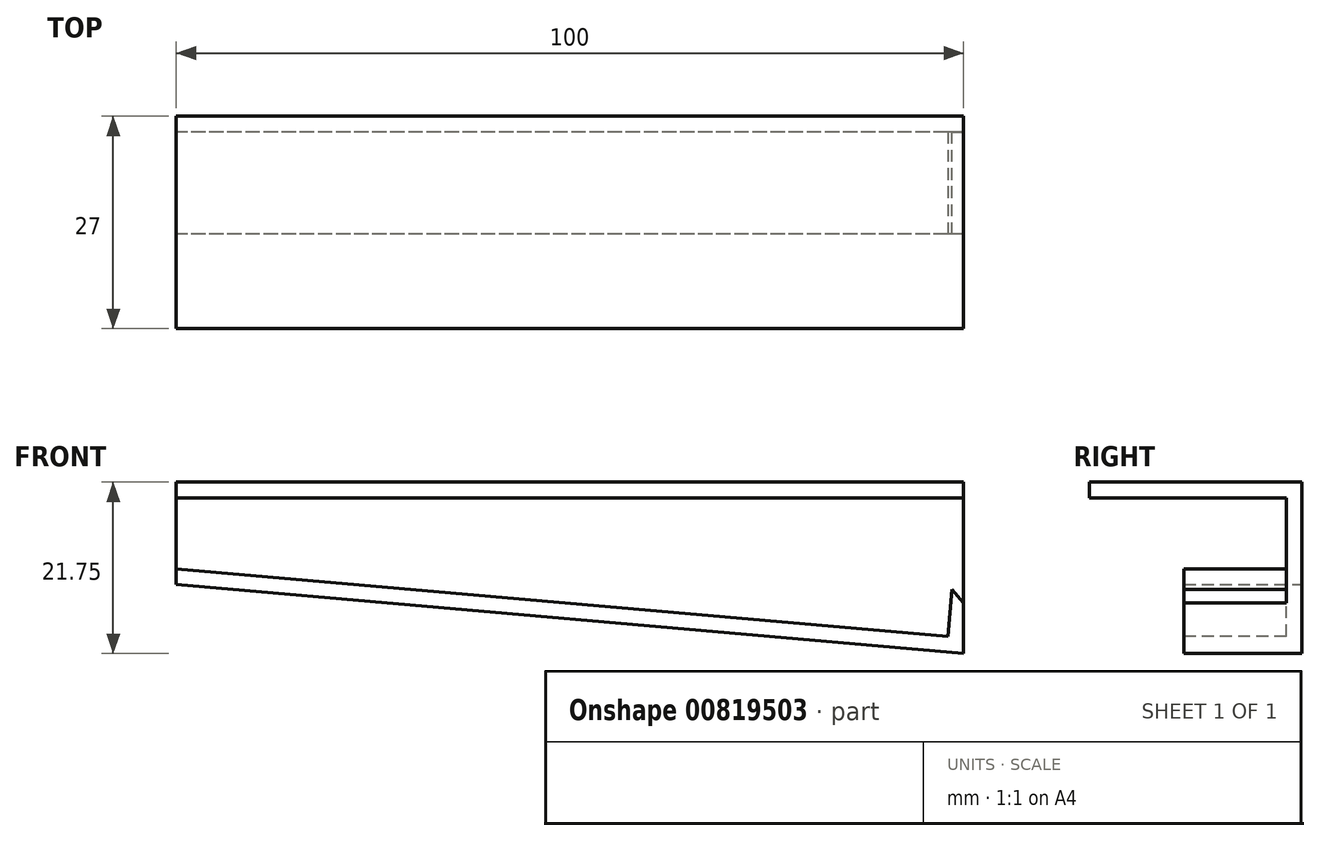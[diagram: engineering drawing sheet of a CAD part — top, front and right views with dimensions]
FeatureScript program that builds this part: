
annotation { "Feature Type Name" : "Feature", "Feature Type Description" : "" }
export const myFeature = defineFeature(function(context is Context, id is Id, definition is map)
    precondition{}
    {
        {
            var Q0;
            Q0=qCreatedBy(makeId("Front.planeOp"),FACE);
            var sketch = newSketch(context, id + "F0", { "sketchPlane" : qUnion([Q0])});
            skLineSegment(sketch, "E0", {"start": v(-26.66, 0) * mm, "end": v(-26.66, 13) * mm});
            skLineSegment(sketch, "E1", {"start": v(-26.66, 13) * mm, "end": v(73.34, 13) * mm});
            skLineSegment(sketch, "E2", {"start": v(73.34, 13) * mm, "end": v(73.34, -8.75) * mm});
            skLineSegment(sketch, "E3", {"start": v(73.34, -8.75) * mm, "end": v(-26.66, 0) * mm});
            skLineSegment(sketch, "E4", {"start": v(-26.66, 0) * mm, "end": v(38.37, 0) * mm, "construction": true});
            skSolve(sketch);
        }
        {
            var Q0;
            Q0=makeQuery(id+"F0.imprint","IMPRINT",FACE,{"disambiguationData":[TD([[makeQuery(id+"F0.imprint","IMPRINT",EDGE,{"derivedFrom":sQuery(id+"F0.wireOp",EDGE,"E0")}),-1.0]])]});
            extrude(context, id + "F1", {"entities" : qUnion([Q0]), "depth" : 2 * mm, "offsetDistance" : 25 * mm});
        }
        {
            var Q0;
            Q0=makeQuery(id+"F1.opExtrude","CAP_FACE",FACE,{"disambiguationData":[OSD([sQuery(id+"F0.wireOp",EDGE,"E0"),sQuery(id+"F0.wireOp",EDGE,"E1"),sQuery(id+"F0.wireOp",EDGE,"E2"),sQuery(id+"F0.wireOp",EDGE,"E3")])],"isStart":false});
            var sketch = newSketch(context, id + "F2", { "sketchPlane" : qUnion([Q0])});
            skLineSegment(sketch, "E5", {"start": v(-26.66, 13) * mm, "end": v(73.34, 13) * mm});
            skLineSegment(sketch, "E6", {"start": v(73.34, 13) * mm, "end": v(73.34, 11) * mm});
            skLineSegment(sketch, "E7", {"start": v(73.34, 11) * mm, "end": v(-26.66, 11) * mm});
            skLineSegment(sketch, "E8", {"start": v(-26.66, 11) * mm, "end": v(-26.66, 13) * mm});
            skLineSegment(sketch, "E9.0", {"start": v(73.34, -6.74) * mm, "end": v(-26.66, 2) * mm});
            skLineSegment(sketch, "E10", {"start": v(73.34, -6.74) * mm, "end": v(73.34, -8.75) * mm});
            skLineSegment(sketch, "E11", {"start": v(73.34, -8.75) * mm, "end": v(-26.66, 0) * mm});
            skLineSegment(sketch, "E12", {"start": v(-26.66, 0) * mm, "end": v(-26.66, 2) * mm});
            skSolve(sketch);
        }
        {
            var Q0;
            Q0=makeQuery(id+"F2.imprint","IMPRINT",FACE,{"disambiguationData":[TD([[makeQuery(id+"F2.imprint","IMPRINT",EDGE,{"derivedFrom":sQuery(id+"F2.wireOp",EDGE,"E9.0")}),1.0]])]});
            extrude(context, id + "F3", {"entities" : qUnion([Q0]), "operationType" : NewBodyOperationType.ADD, "depth" : 13 * mm, "offsetDistance" : 25 * mm});
        }
        {
            var Q0;
            Q0=makeQuery(id+"F2.imprint","IMPRINT",FACE,{"disambiguationData":[TD([[makeQuery(id+"F2.imprint","IMPRINT",EDGE,{"derivedFrom":sQuery(id+"F2.wireOp",EDGE,"E5")}),-1.0]])]});
            extrude(context, id + "F4", {"entities" : qUnion([Q0]), "operationType" : NewBodyOperationType.ADD, "depth" : 25 * mm, "offsetDistance" : 25 * mm});
        }
        {
            var Q0;
            Q0=makeQuery(id+"F3.opExtrude","SWEPT_FACE",FACE,{"disambiguationData":[OSD([sQuery(id+"F2.wireOp",EDGE,"E9.0")])]});
            var sketch = newSketch(context, id + "F5", { "sketchPlane" : qUnion([Q0])});
            skLineSegment(sketch, "E13.bottom", {"start": v(73.64, -2) * mm, "end": v(71.66, -2) * mm});
            skLineSegment(sketch, "E13.top", {"start": v(73.64, -15) * mm, "end": v(71.66, -15) * mm});
            skLineSegment(sketch, "E13.left", {"start": v(73.64, -2) * mm, "end": v(73.64, -15) * mm});
            skLineSegment(sketch, "E13.right", {"start": v(71.66, -2) * mm, "end": v(71.66, -15) * mm});
            skSolve(sketch);
        }
        {
            var Q0;
            Q0=makeQuery(id+"F5.imprint","IMPRINT",FACE,{"disambiguationData":[TD([[makeQuery(id+"F5.imprint","IMPRINT",EDGE,{"derivedFrom":sQuery(id+"F5.wireOp",EDGE,"E13.bottom")}),1.0]])]});
            extrude(context, id + "F6", {"entities" : qUnion([Q0]), "operationType" : NewBodyOperationType.ADD, "depth" : 6 * mm, "offsetDistance" : 25 * mm});
        }
        {
            var Q0;
            Q0=makeQuery(id+"F6.opExtrude","CAP_EDGE",EDGE,{"disambiguationData":[OSD([sQuery(id+"F5.wireOp",EDGE,"E13.left")])],"isStart":false});
            chamfer(context, id + "F7", {"entities" : qUnion([Q0]), "width" : 2 * mm, "tangentPropagation" : true});
        }
        {
            var Q0;
            Q0=makeQuery(id+"F6.opExtrude","SWEPT_FACE",FACE,{"disambiguationData":[OSD([sQuery(id+"F5.wireOp",EDGE,"E13.bottom")])]});
            var sketch = newSketch(context, id + "F8", { "sketchPlane" : qUnion([Q0])});
            skLineSegment(sketch, "E14.0.0", {"start": v(-73.34, -6.74) * mm, "end": v(-73.34, -2.34) * mm});
            skLineSegment(sketch, "E14.0.1", {"start": v(-73.34, -2.34) * mm, "end": v(-73.68, -2.76) * mm});
            skLineSegment(sketch, "E14.0.2", {"start": v(-73.68, -2.76) * mm, "end": v(-73.34, -6.74) * mm});
            skSolve(sketch);
        }
        {
            var Q0;
            Q0=makeQuery(id+"F8.imprint","IMPRINT",FACE,{"disambiguationData":[TD([[makeQuery(id+"F8.imprint","IMPRINT",EDGE,{"derivedFrom":sQuery(id+"F8.wireOp",EDGE,"E14.0.0")}),-1.0]])]});
            extrude(context, id + "F9", {"entities" : qUnion([Q0]), "operationType" : NewBodyOperationType.REMOVE, "oppositeDirection" : true, "depth" : 25 * mm, "offsetDistance" : 25 * mm});
        }
    });
